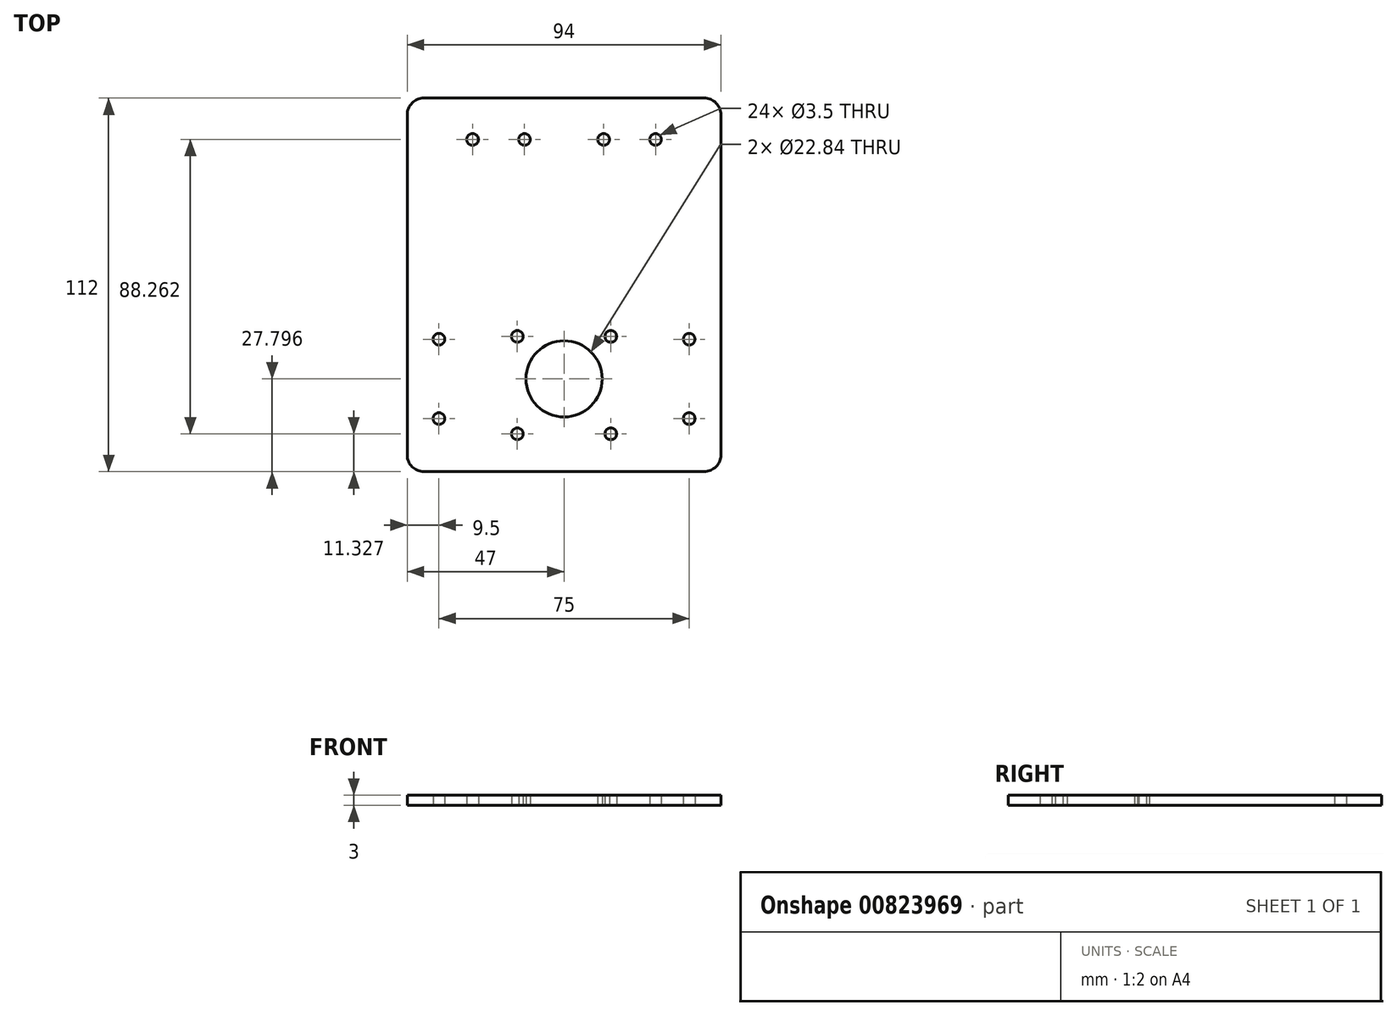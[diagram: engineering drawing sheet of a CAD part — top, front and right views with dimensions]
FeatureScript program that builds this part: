
annotation { "Feature Type Name" : "Feature", "Feature Type Description" : "" }
export const myFeature = defineFeature(function(context is Context, id is Id, definition is map)
    precondition{}
    {
        {
            var Q0;
            Q0=qCreatedBy(makeId("Top.planeOp"),FACE);
            var sketch = newSketch(context, id + "F0", { "sketchPlane" : qUnion([Q0])});
            skLineSegment(sketch, "E0.bottom", {"start": v(42, -56) * mm, "end": v(-42, -56) * mm});
            skLineSegment(sketch, "E0.top", {"start": v(42, 56) * mm, "end": v(-42, 56) * mm});
            skLineSegment(sketch, "E0.left", {"start": v(47, -51) * mm, "end": v(47, 51) * mm});
            skLineSegment(sketch, "E0.right", {"start": v(-47, -51) * mm, "end": v(-47, 51) * mm});
            skPoint(sketch, "E0.middle", {"position": v(0, 0) * mm});
            skPoint(sketch, "E1.visualSharp", {"position": v(-47, 56) * mm});
            skArc(sketch, "E1.filletArc", {"start": v(-42, 56) * mm, "mid": v(-45.54, 54.54) * mm, "end": v(-47, 51) * mm});
            skPoint(sketch, "E2.visualSharp", {"position": v(47, 56) * mm});
            skArc(sketch, "E2.filletArc", {"start": v(47, 51) * mm, "mid": v(45.54, 54.54) * mm, "end": v(42, 56) * mm});
            skPoint(sketch, "E3.visualSharp", {"position": v(47, -56) * mm});
            skArc(sketch, "E3.filletArc", {"start": v(42, -56) * mm, "mid": v(45.54, -54.54) * mm, "end": v(47, -51) * mm});
            skPoint(sketch, "E4.visualSharp", {"position": v(-47, -56) * mm});
            skArc(sketch, "E4.filletArc", {"start": v(-47, -51) * mm, "mid": v(-45.54, -54.54) * mm, "end": v(-42, -56) * mm});
            skCircle(sketch, "E5", {"center": v(11.86, 43.59) * mm, "radius": 1.75 * mm});
            skCircle(sketch, "E6", {"center": v(37.5, -16.3) * mm, "radius": 1.75 * mm});
            skCircle(sketch, "E7", {"center": v(37.5, -40.1) * mm, "radius": 1.75 * mm});
            skCircle(sketch, "E8", {"center": v(27.42, 43.59) * mm, "radius": 1.75 * mm});
            skCircle(sketch, "E9", {"center": v(0, -28.2) * mm, "radius": 11.42 * mm});
            skCircle(sketch, "E10", {"center": v(14, -15.46) * mm, "radius": 1.75 * mm});
            skCircle(sketch, "E11", {"center": v(14, -44.67) * mm, "radius": 1.75 * mm});
            skCircle(sketch, "E12.MirrorC", {"center": v(-11.86, 43.59) * mm, "radius": 1.75 * mm});
            skCircle(sketch, "E13.MirrorC", {"center": v(-27.42, 43.59) * mm, "radius": 1.75 * mm});
            skCircle(sketch, "E14.MirrorC", {"center": v(-14, -15.46) * mm, "radius": 1.75 * mm});
            skCircle(sketch, "E15.MirrorC", {"center": v(-14, -44.67) * mm, "radius": 1.75 * mm});
            skCircle(sketch, "E16.MirrorC", {"center": v(-37.5, -40.1) * mm, "radius": 1.75 * mm});
            skCircle(sketch, "E17.MirrorC", {"center": v(-37.5, -16.3) * mm, "radius": 1.75 * mm});
            skLineSegment(sketch, "E18", {"start": v(-37.5, -16.3) * mm, "end": v(-37.5, -40.1) * mm, "construction": true});
            skLineSegment(sketch, "E19", {"start": v(-37.5, -28.2) * mm, "end": v(0, -28.2) * mm, "construction": true});
            skSolve(sketch);
        }
        {
            var Q0;
            Q0=qSketchRegion(id+"F0",true);
            extrude(context, id + "F1", {"entities" : qUnion([Q0]), "depth" : 3 * mm, "offsetDistance" : 25 * mm});
        }
    });
